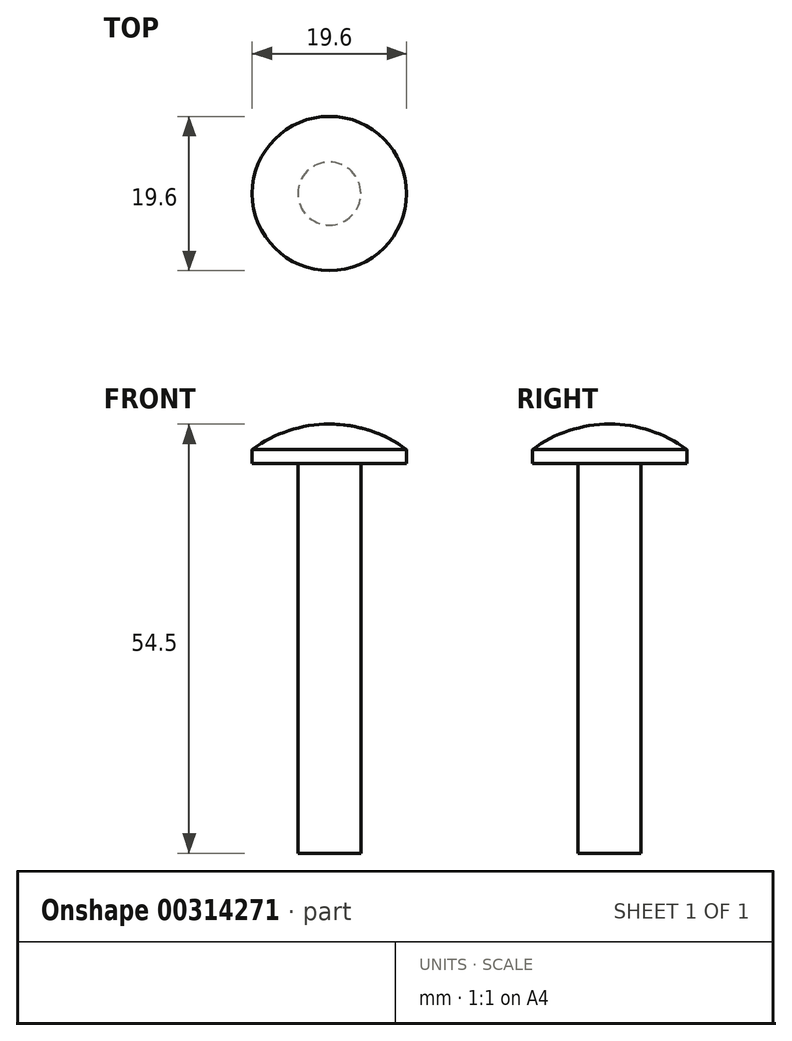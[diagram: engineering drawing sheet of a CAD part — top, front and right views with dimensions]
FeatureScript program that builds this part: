
annotation { "Feature Type Name" : "Feature", "Feature Type Description" : "" }
export const myFeature = defineFeature(function(context is Context, id is Id, definition is map)
    precondition{}
    {
        {
            var Q0;
            Q0=qCreatedBy(makeId("Front.planeOp"),FACE);
            var sketch = newSketch(context, id + "F0", { "sketchPlane" : qUnion([Q0])});
            skLineSegment(sketch, "E0", {"start": v(0, 0) * mm, "end": v(0, -54.5) * mm});
            skLineSegment(sketch, "E1", {"start": v(0, -54.5) * mm, "end": v(4, -54.5) * mm});
            skLineSegment(sketch, "E2", {"start": v(0, -5) * mm, "end": v(9.8, -5) * mm, "construction": true});
            skLineSegment(sketch, "E3", {"start": v(9.8, -5) * mm, "end": v(9.8, -3.2) * mm});
            skLineSegment(sketch, "E4", {"start": v(0, 0) * mm, "end": v(-5, 0) * mm, "construction": true});
            skArc(sketch, "E5", {"start": v(9.8, -3.2) * mm, "mid": v(5.15, -0.82) * mm, "end": v(0, 0) * mm});
            skLineSegment(sketch, "E6", {"start": v(4, -54.5) * mm, "end": v(4, -5) * mm});
            skLineSegment(sketch, "E7", {"start": v(4, -5) * mm, "end": v(9.8, -5) * mm});
            skSolve(sketch);
        }
        {
            var Q0;
            Q0 = qSketchRegion(id + "F0", true);
            var Q1;
            Q1 = qConstructionFilter(qBodyType(qCreatedBy(id + "F0" ,EDGE), BodyType.WIRE), ConstructionObject.NO);
            var Q2;
            Q2=sQuery(id+"F0.wireOp",EDGE,"E0");
            revolve(context, id + "F1", {"entities" : qUnion([Q0]), "surfaceEntities" : qUnion([Q1]), "axis" : qUnion([Q2]), "revolveType" : RevolveType.FULL});
        }
    });
